# Revit family: LTC-4RDW-W
name_source: partatom
category: Lighting Fixtures
revit_build: Autodesk Revit 2014 (Build: 20130308_1515(x64)
units: mm (PartAtom-declared; Revit-internal decimal feet)

## types (1)
- LTC-4RDW-W
    Apparent Load = 72 VA
    Backbox = Hubbell - Matt Black
    Ballast = Paint - Hubbell - Carbon Black
    Certifications = • cCSAus certified to UL 1598
• Wall Mount: Suitable for wet locations
• Surface & Pendant Mount: Suitable for wet
locations under covered ceiling
• Cord Mount and all Wall Wash: Suitable for
damp locations
    Color Filter = 16777215
    Cord Height = 72 "
    Default Elevation = 48 "
    Description = LITEISTRY™ 6inch Round Cylinder Downlight/Wall Wash
    Dimming Lamp Color Temperature Shift = <None>
    Emit Shape Visible in Rendering = No
    Emit from Circle Diameter = 5.6 "
    Features = • 4inch architectural LED downlight and wall wash cylinder
delivering 600 - 7000 lm
• 4 beam distributions from 0.3 to 1.1 Spacing Criteria
• Quiet reflector appearance with 50º optical cutoff
• 2700K - 5000K, 80+ and 90+ CRI options
• Available in Surface, Wall, Pendant, or Cord Mount configurations
• Variety of dimming protocol options including 0-10V, DALI, DMX,
Forward Phase and EcoSystem
    Lamp = LED Lamp
    Manufacturer = Prescolite
    Model = LTC-4RDW
    Photometric Web File = LTC-6RD-P-20L35K8MD-DM1-S-BL.ies
    Product Documentation Link = https://hubbellcdn.com
    Product Page URL = https://www.hubbell.com
    Reflector = Glass - Hubbell - Glass
    Tilt Angle = -90.00°
    URL = http://www.prescolite.com
    Voltage = 120 V
    Warranty = • 5 year warranty
• See HLI Standard Warranty for
additional information

## geometry (parser evidence)
native form markers: Blend x12, Sweep x3
no freeform markers — native parametric forms only
